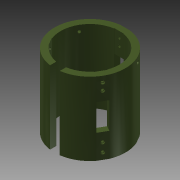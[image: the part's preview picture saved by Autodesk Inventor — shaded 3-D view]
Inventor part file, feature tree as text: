
AUTODESK INVENTOR PART (.ipt)
format: ipt  version: 2013 (Build 170138000, 138)  size: 443,904 bytes
history: native  units: mm
features: sketch x21, extrude x15, other x6, pattern_circular x5, hole x4
ambient origin geometry x8: Origin, YZ Plane, XZ Plane, XY Plane, X Axis, Y Axis, Z Axis, Center Point
feature tree (51):
  other  "ソリッド1"
  extrude  "押し出し1"  Depth=26.0mm
  extrude  "押し出し2"  Depth=20.0mm
  hole  "穴1"  [1 undecoded]
  pattern_circular  "円形状パターン1"  [2 undecoded]
  sketch  "スケッチ4"
  other  "作業平面1"
  other  "作業平面3"
  other  "作業平面7"
  extrude  "押し出し3"  Depth=10.8mm
  pattern_circular  "円形状パターン2"  [2 undecoded]
  other  "作業平面8"
  hole  "穴2"  [1 undecoded]
  pattern_circular  "円形状パターン3"  Count=3 Angle=360.0deg
  extrude  "押し出し4"  Depth=19.5mm
  extrude  "押し出し5"  Depth=4.7mm
  extrude  "押し出し6"  Depth=50.6mm
  extrude  "押し出し7"  Depth=3.0mm
  sketch  "スケッチ11"
  other  "作業平面9"
  extrude  "押し出し8"  Depth=3.0mm
  extrude  "押し出し9"  Depth=5.1mm
  extrude  "押し出し10"  Depth=4.7mm
  extrude  "押し出し11"  Depth=3.0mm
  extrude  "押し出し12"  Depth=50.6mm
  hole  "穴3"  [1 undecoded]
  extrude  "押し出し13"  Depth=30.0mm TaperAngle=360.0deg
  extrude  "押し出し14"  Depth=60.0mm TaperAngle=360.0deg
  extrude  "押し出し15"  Depth=24.2mm
  hole  "穴4"  [1 undecoded]
  pattern_circular  "円形状パターン4"  [2 undecoded]
  pattern_circular  "円形状パターン5"  [2 undecoded]
  sketch  "スケッチ1"
  sketch  "スケッチ2"
  sketch  "スケッチ3"
  sketch  "スケッチ5"
  sketch  "スケッチ6"
  sketch  "スケッチ7"
  sketch  "スケッチ8"
  sketch  "スケッチ9"
  sketch  "スケッチ10"
  sketch  "スケッチ12"
  sketch  "スケッチ13"
  sketch  "スケッチ14"
  sketch  "スケッチ15"
  sketch  "スケッチ16"
  sketch  "スケッチ17"
  sketch  "スケッチ18"
  sketch  "スケッチ19"
  sketch  "スケッチ20"
  sketch  "スケッチ21"
note: 12 required parameter values undecoded (feature->parameter linkage not recoverable at this tier; creation-order binding heuristic only, values carry confidence <= 0.55)
